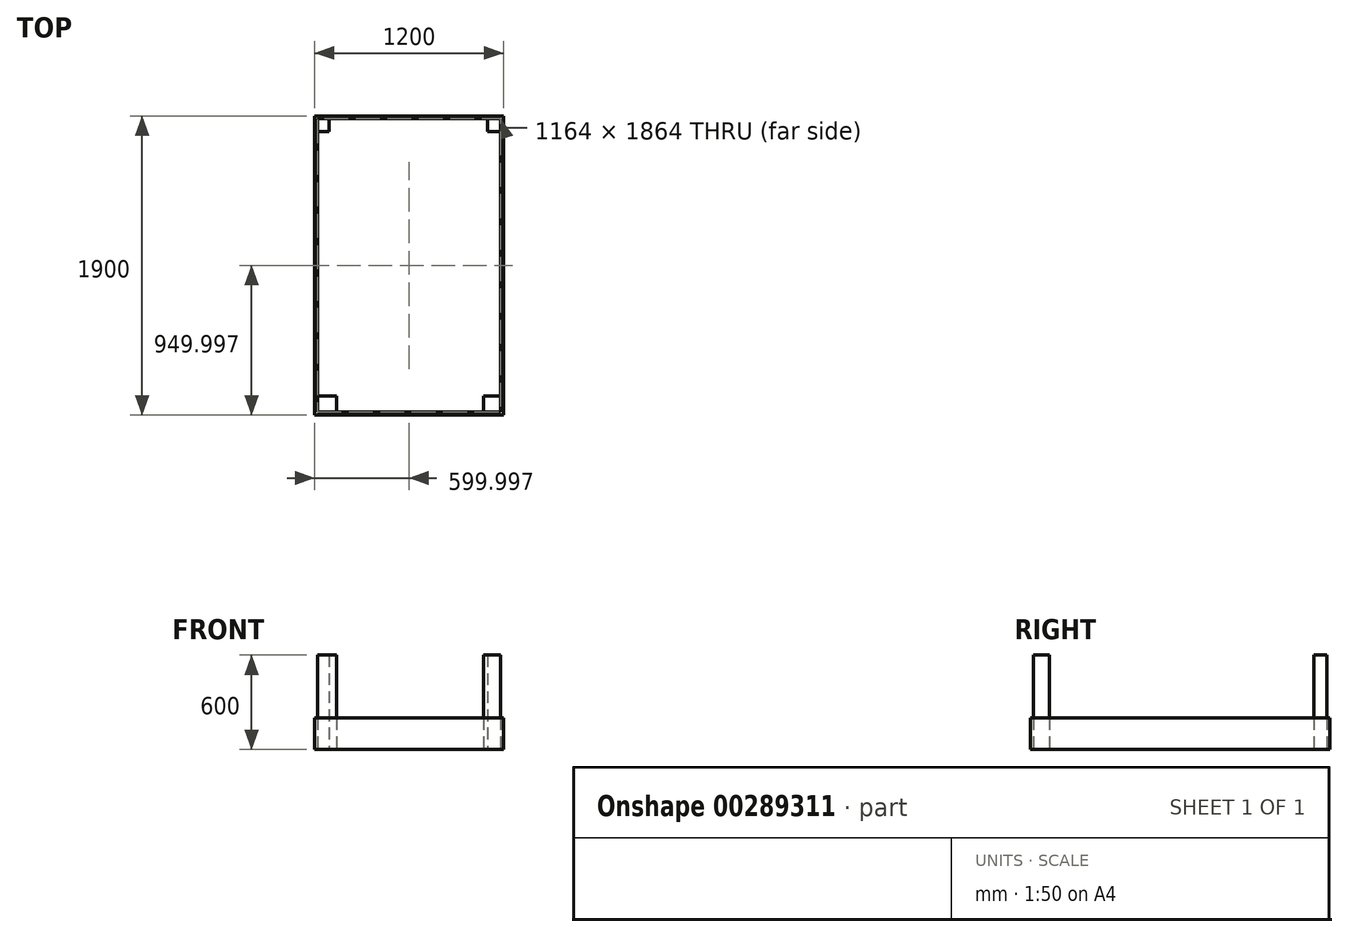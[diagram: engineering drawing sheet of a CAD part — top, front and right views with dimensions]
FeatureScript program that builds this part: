
annotation { "Feature Type Name" : "Feature", "Feature Type Description" : "" }
export const myFeature = defineFeature(function(context is Context, id is Id, definition is map)
    precondition{}
    {
        {
            var Q0;
            Q0=qCreatedBy(makeId("Top.planeOp"),FACE);
            var sketch = newSketch(context, id + "F0", { "sketchPlane" : qUnion([Q0])});
            skLineSegment(sketch, "E0.bottom", {"start": v(-57.93, 1779.24) * mm, "end": v(1142.07, 1779.24) * mm});
            skLineSegment(sketch, "E0.top", {"start": v(-57.93, -120.76) * mm, "end": v(1142.07, -120.76) * mm});
            skLineSegment(sketch, "E0.left", {"start": v(-57.93, 1779.24) * mm, "end": v(-57.93, -120.76) * mm});
            skLineSegment(sketch, "E0.right", {"start": v(1142.07, 1779.24) * mm, "end": v(1142.07, -120.76) * mm});
            skLineSegment(sketch, "E1.0", {"start": v(-39.93, 1761.24) * mm, "end": v(1124.07, 1761.24) * mm});
            skLineSegment(sketch, "E1.1", {"start": v(-39.93, 1761.24) * mm, "end": v(-39.93, -102.76) * mm});
            skLineSegment(sketch, "E1.2", {"start": v(-39.93, -102.76) * mm, "end": v(1124.07, -102.76) * mm});
            skLineSegment(sketch, "E1.3", {"start": v(1124.07, 1761.24) * mm, "end": v(1124.07, -102.76) * mm});
            skLineSegment(sketch, "E2.bottom", {"start": v(-39.93, 1680.54) * mm, "end": v(1124.07, 1680.54) * mm});
            skLineSegment(sketch, "E2.top", {"start": v(-39.93, 1628.68) * mm, "end": v(1124.07, 1628.68) * mm});
            skLineSegment(sketch, "E2.left", {"start": v(-39.93, 1680.54) * mm, "end": v(-39.93, 1628.68) * mm});
            skLineSegment(sketch, "E2.right", {"start": v(1124.07, 1680.54) * mm, "end": v(1124.07, 1628.68) * mm});
            skLineSegment(sketch, "E3.bottom", {"start": v(-39.93, 1519.8) * mm, "end": v(1124.07, 1519.8) * mm});
            skLineSegment(sketch, "E3.top", {"start": v(-39.93, 1461.03) * mm, "end": v(1124.07, 1461.03) * mm});
            skLineSegment(sketch, "E3.left", {"start": v(-39.93, 1519.8) * mm, "end": v(-39.93, 1461.03) * mm});
            skLineSegment(sketch, "E3.right", {"start": v(1124.07, 1519.8) * mm, "end": v(1124.07, 1461.03) * mm});
            skLineSegment(sketch, "E4.bottom", {"start": v(-39.93, 1219.44) * mm, "end": v(1124.07, 1219.44) * mm});
            skLineSegment(sketch, "E4.top", {"start": v(-39.93, 1126.32) * mm, "end": v(1124.07, 1126.32) * mm});
            skLineSegment(sketch, "E4.left", {"start": v(-39.93, 1219.44) * mm, "end": v(-39.93, 1126.32) * mm});
            skLineSegment(sketch, "E4.right", {"start": v(1124.07, 1219.44) * mm, "end": v(1124.07, 1126.32) * mm});
            skLineSegment(sketch, "E5.bottom", {"start": v(-39.93, 695.62) * mm, "end": v(1124.07, 695.62) * mm});
            skLineSegment(sketch, "E5.top", {"start": v(-39.93, 567.58) * mm, "end": v(1124.07, 567.58) * mm});
            skLineSegment(sketch, "E5.left", {"start": v(-39.93, 695.62) * mm, "end": v(-39.93, 567.58) * mm});
            skLineSegment(sketch, "E5.right", {"start": v(1124.07, 695.62) * mm, "end": v(1124.07, 567.58) * mm});
            skLineSegment(sketch, "E6.bottom", {"start": v(-39.93, 280.45) * mm, "end": v(1124.07, 280.45) * mm});
            skLineSegment(sketch, "E6.top", {"start": v(-39.93, 160.17) * mm, "end": v(1124.07, 160.17) * mm});
            skLineSegment(sketch, "E6.left", {"start": v(-39.93, 280.45) * mm, "end": v(-39.93, 160.17) * mm});
            skLineSegment(sketch, "E6.right", {"start": v(1124.07, 280.45) * mm, "end": v(1124.07, 160.17) * mm});
            skLineSegment(sketch, "E7.bottom", {"start": v(-57.93, 1779.24) * mm, "end": v(34.13, 1779.24) * mm});
            skLineSegment(sketch, "E7.top", {"start": v(-57.93, 1680.54) * mm, "end": v(34.13, 1680.54) * mm});
            skLineSegment(sketch, "E7.left", {"start": v(-57.93, 1779.24) * mm, "end": v(-57.93, 1680.54) * mm});
            skLineSegment(sketch, "E7.right", {"start": v(34.13, 1779.24) * mm, "end": v(34.13, 1680.54) * mm});
            skLineSegment(sketch, "E8.bottom", {"start": v(1142.07, 1779.24) * mm, "end": v(1124.07, 1779.24) * mm});
            skLineSegment(sketch, "E8.top", {"start": v(1142.07, 1680.54) * mm, "end": v(1124.07, 1680.54) * mm});
            skLineSegment(sketch, "E8.left", {"start": v(1142.07, 1779.24) * mm, "end": v(1142.07, 1680.54) * mm});
            skLineSegment(sketch, "E8.right", {"start": v(1124.07, 1779.24) * mm, "end": v(1124.07, 1680.54) * mm});
            skLineSegment(sketch, "E9.bottom", {"start": v(1142.07, 1779.24) * mm, "end": v(1039.08, 1779.24) * mm});
            skLineSegment(sketch, "E9.top", {"start": v(1142.07, 1680.54) * mm, "end": v(1039.08, 1680.54) * mm});
            skLineSegment(sketch, "E9.right", {"start": v(1039.08, 1779.24) * mm, "end": v(1039.08, 1680.54) * mm});
            skLineSegment(sketch, "E10.bottom", {"start": v(-57.93, -120.76) * mm, "end": v(80.69, -120.76) * mm});
            skLineSegment(sketch, "E10.top", {"start": v(-57.93, 0) * mm, "end": v(80.69, 0) * mm});
            skLineSegment(sketch, "E10.left", {"start": v(-57.93, -120.76) * mm, "end": v(-57.93, 0) * mm});
            skLineSegment(sketch, "E10.right", {"start": v(80.69, -120.76) * mm, "end": v(80.69, 0) * mm});
            skLineSegment(sketch, "E11.bottom", {"start": v(1142.07, -120.76) * mm, "end": v(1015.8, -120.76) * mm});
            skLineSegment(sketch, "E11.top", {"start": v(1142.07, 0) * mm, "end": v(1015.8, 0) * mm});
            skLineSegment(sketch, "E11.left", {"start": v(1142.07, -120.76) * mm, "end": v(1142.07, 0) * mm});
            skLineSegment(sketch, "E11.right", {"start": v(1015.8, -120.76) * mm, "end": v(1015.8, 0) * mm});
            skSolve(sketch);
        }
        {
            var Q0;
            {var subQ0=sQuery(id+"F0.wireOp",EDGE,"E1.1");var subQ1=sQuery(id+"F0.wireOp",EDGE,"E1.0");var subQ2=makeQuery(id+"F0.imprint","INTERSECT",VERTEX,{"derivedFrom":[subQ1,subQ0]});Q0=makeQuery(id+"F0.imprint","IMPRINT",FACE,{"disambiguationData":[TD([[makeQuery(id+"F0.imprint","IMPRINT",EDGE,{"disambiguationData":[TD([[subQ2,-1.0]])],"derivedFrom":subQ1}),-1.0]])]});}
            var Q1;
            {var subQ0=sQuery(id+"F0.wireOp",EDGE,"E8.right");var subQ1=sQuery(id+"F0.wireOp",EDGE,"E1.0");var subQ2=makeQuery(id+"F0.imprint","INTERSECT",VERTEX,{"derivedFrom":[subQ1,subQ0]});Q1=makeQuery(id+"F0.imprint","IMPRINT",FACE,{"disambiguationData":[TD([[makeQuery(id+"F0.imprint","IMPRINT",EDGE,{"disambiguationData":[TD([[subQ2,1.0]])],"derivedFrom":subQ1}),-1.0]])]});}
            var Q2;
            {var subQ0=sQuery(id+"F0.wireOp",EDGE,"E1.2");var subQ1=sQuery(id+"F0.wireOp",EDGE,"E1.1");var subQ2=makeQuery(id+"F0.imprint","INTERSECT",VERTEX,{"derivedFrom":[subQ1,subQ0]});Q2=makeQuery(id+"F0.imprint","IMPRINT",FACE,{"disambiguationData":[TD([[makeQuery(id+"F0.imprint","IMPRINT",EDGE,{"disambiguationData":[TD([[subQ2,1.0]])],"derivedFrom":subQ1}),1.0]])]});}
            var Q3;
            {var subQ0=sQuery(id+"F0.wireOp",EDGE,"E1.3");var subQ1=sQuery(id+"F0.wireOp",EDGE,"E1.2");var subQ2=makeQuery(id+"F0.imprint","INTERSECT",VERTEX,{"derivedFrom":[subQ1,subQ0]});Q3=makeQuery(id+"F0.imprint","IMPRINT",FACE,{"disambiguationData":[TD([[makeQuery(id+"F0.imprint","IMPRINT",EDGE,{"disambiguationData":[TD([[subQ2,1.0]])],"derivedFrom":subQ1}),1.0]])]});}
            extrude(context, id + "F1", {"entities" : qUnion([Q0, Q1, Q2, Q3]), "depth" : 600 * mm});
        }
        {
            var Q0;
            Q0 = qSketchRegion(id + "F0", true);
            extrude(context, id + "F2", {"entities" : qUnion([Q0]), "depth" : 200 * mm});
        }
    });
